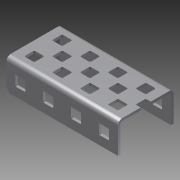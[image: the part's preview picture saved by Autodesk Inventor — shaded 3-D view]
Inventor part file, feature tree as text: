
AUTODESK INVENTOR PART (.ipt)
format: ipt  version: 2014 SP1 (Build 180222100, 222)  size: 346,112 bytes
history: native  units: in
note: dims shown in document units (in); Inventor stores cm internally (conversion verified against a paired STEP export)
features: other x1, imported_body x1, extrude x1, sketch x1
ambient origin geometry x8: Origin, YZ Plane, XZ Plane, XY Plane, X Axis, Y Axis, Z Axis, Center Point
bodies: Body1 (feature_tree)
feature tree (4):
  parser-record x1  (decoder bookkeeping rows leaked as tree rows — omitted from the tree; the rows remain in map.json)
  imported_body  "Base1"
  extrude  "Extrusion1"  Depth=1.0in TaperAngle=0.0deg
  sketch  "Sketch1"  dims[d0=0.5in d1=1.0in d2=0.0in]
